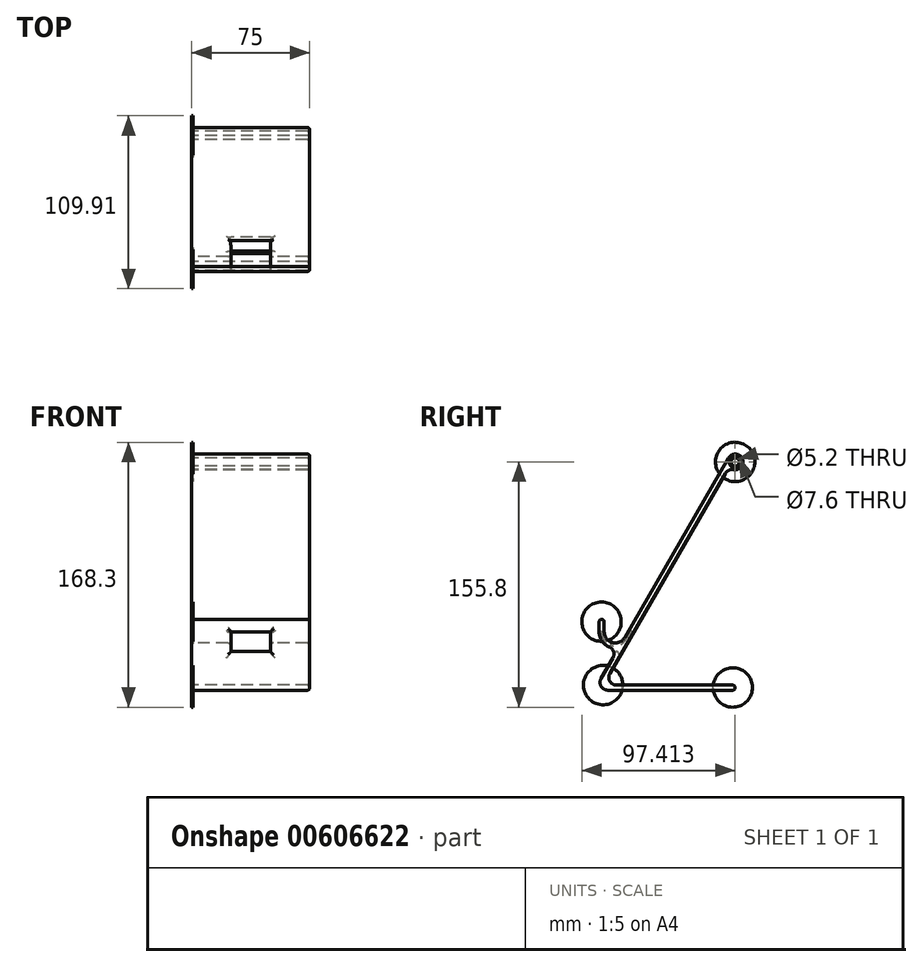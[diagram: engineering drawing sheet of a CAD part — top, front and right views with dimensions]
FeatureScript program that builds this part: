
annotation { "Feature Type Name" : "Feature", "Feature Type Description" : "" }
export const myFeature = defineFeature(function(context is Context, id is Id, definition is map)
    precondition{}
    {
        {
            var Q0;
            Q0=qCreatedBy(makeId("Right.planeOp"),FACE);
            var sketch = newSketch(context, id + "F0", { "sketchPlane" : qUnion([Q0])});
            skLineSegment(sketch, "E0.2", {"start": v(-43.92, -30) * mm, "end": v(-43.92, -38) * mm});
            skArc(sketch, "E0.4", {"start": v(-43.92, -38) * mm, "mid": v(-42.2, -43.67) * mm, "end": v(-37.61, -47.43) * mm});
            skLineSegment(sketch, "E1.2", {"start": v(-40.72, -30) * mm, "end": v(-40.72, -38) * mm});
            skLineSegment(sketch, "E1.3", {"start": v(-27.66, -41.5) * mm, "end": v(38.16, 72.5) * mm});
            skArc(sketch, "E2.filletArc", {"start": v(-40.72, -38) * mm, "mid": v(-35.53, -44.76) * mm, "end": v(-27.66, -41.5) * mm});
            skLineSegment(sketch, "E3", {"start": v(-43.92, -30) * mm, "end": v(-40.72, -30) * mm});
            skLineSegment(sketch, "E4", {"start": v(-42.67, -67.5) * mm, "end": v(-35.19, -54.55) * mm});
            skLineSegment(sketch, "E5.bottom", {"start": v(-38.34, -75) * mm, "end": v(42.5, -75) * mm});
            skLineSegment(sketch, "E5.top", {"start": v(-32.8, -71.8) * mm, "end": v(42.5, -71.8) * mm});
            skLineSegment(sketch, "E5.right", {"start": v(42.5, -75) * mm, "end": v(42.5, -71.8) * mm});
            skLineSegment(sketch, "E6", {"start": v(-37.12, -64.3) * mm, "end": v(36.2, 62.7) * mm});
            skPoint(sketch, "E7", {"position": v(0, 0) * mm});
            skArc(sketch, "E8", {"start": v(38.16, 72.5) * mm, "mid": v(47.05, 72.06) * mm, "end": v(41.51, 65.1) * mm});
            skPoint(sketch, "E9.visualSharp", {"position": v(-31.36, -47.92) * mm});
            skArc(sketch, "E9.filletArc", {"start": v(-35.19, -54.55) * mm, "mid": v(-34.79, -50.44) * mm, "end": v(-37.61, -47.43) * mm});
            skArc(sketch, "E10.filletArc", {"start": v(-37.12, -64.3) * mm, "mid": v(-37.12, -69.3) * mm, "end": v(-32.8, -71.8) * mm});
            skArc(sketch, "E11.filletArc", {"start": v(-42.67, -67.5) * mm, "mid": v(-42.67, -72.5) * mm, "end": v(-38.34, -75) * mm});
            skArc(sketch, "E12", {"start": v(41.51, 65.1) * mm, "mid": v(38.47, 64.75) * mm, "end": v(36.2, 62.7) * mm});
            skCircle(sketch, "E13", {"center": v(42.5, 70) * mm, "radius": 2.6 * mm});
            skSolve(sketch);
        }
        {
            var Q0;
            Q0=qSketchRegion(id+"F0",true);
            extrude(context, id + "F1", {"entities" : qUnion([Q0]), "endBound" : BoundingType.SYMMETRIC, "depth" : 75 * mm, "offsetDistance" : 25 * mm});
        }
        {
            var Q0;
            Q0=makeQuery(id+"F1.opExtrude","SWEPT_FACE",FACE,{"disambiguationData":[OSD([sQuery(id+"F0.wireOp",EDGE,"E0.2")])]});
            var sketch = newSketch(context, id + "F2", { "sketchPlane" : qUnion([Q0])});
            skLineSegment(sketch, "E14.bottom", {"start": v(-12.5, -38) * mm, "end": v(12.5, -38) * mm});
            skLineSegment(sketch, "E14.top", {"start": v(-12.5, -50.43) * mm, "end": v(12.5, -50.43) * mm});
            skLineSegment(sketch, "E14.left", {"start": v(-12.5, -38) * mm, "end": v(-12.5, -50.43) * mm});
            skLineSegment(sketch, "E14.right", {"start": v(12.5, -38) * mm, "end": v(12.5, -50.43) * mm});
            skSolve(sketch);
        }
        {
            var Q0;
            Q0 = qSketchRegion(id + "F2", true);
            extrude(context, id + "F3", {"entities" : qUnion([Q0]), "operationType" : NewBodyOperationType.REMOVE, "oppositeDirection" : true, "depth" : 25 * mm, "offsetDistance" : 25 * mm});
        }
        {
            var Q0;
            Q0=makeQuery(id+"F1.opExtrude","SWEPT_FACE",FACE,{"disambiguationData":[OSD([sQuery(id+"F0.wireOp",EDGE,"E3")])]});
            var Q1;
            Q1=makeQuery(id+"F1.opExtrude","CAP_FACE",FACE,{"disambiguationData":[OSD([sQuery(id+"F0.wireOp",EDGE,"E0.2"),sQuery(id+"F0.wireOp",EDGE,"E0.4"),sQuery(id+"F0.wireOp",EDGE,"E1.2"),sQuery(id+"F0.wireOp",EDGE,"E1.3"),sQuery(id+"F0.wireOp",EDGE,"E2.filletArc"),sQuery(id+"F0.wireOp",EDGE,"E3"),sQuery(id+"F0.wireOp",EDGE,"OJqH4mra-1SRE-s8op-VV3v-gDYp8EEXXtRn"),sQuery(id+"F0.wireOp",EDGE,"E4"),sQuery(id+"F0.wireOp",EDGE,"E5.bottom"),sQuery(id+"F0.wireOp",EDGE,"E5.top"),sQuery(id+"F0.wireOp",EDGE,"E5.right"),sQuery(id+"F0.wireOp",EDGE,"E6"),sQuery(id+"F0.wireOp",EDGE,"E8"),sQuery(id+"F0.wireOp",EDGE,"jVerfQlz-GGoS-WxWe-SnGt-XEWwIJdHr9bm"),sQuery(id+"F0.wireOp",EDGE,"E9.filletArc"),sQuery(id+"F0.wireOp",EDGE,"E10.filletArc"),sQuery(id+"F0.wireOp",EDGE,"E11.filletArc")])],"isStart":false});
            var Q2;
            Q2=makeQuery(id+"F1.opExtrude","CAP_FACE",FACE,{"disambiguationData":[OSD([sQuery(id+"F0.wireOp",EDGE,"E0.2"),sQuery(id+"F0.wireOp",EDGE,"E0.4"),sQuery(id+"F0.wireOp",EDGE,"E1.2"),sQuery(id+"F0.wireOp",EDGE,"E1.3"),sQuery(id+"F0.wireOp",EDGE,"E2.filletArc"),sQuery(id+"F0.wireOp",EDGE,"E3"),sQuery(id+"F0.wireOp",EDGE,"OJqH4mra-1SRE-s8op-VV3v-gDYp8EEXXtRn"),sQuery(id+"F0.wireOp",EDGE,"E4"),sQuery(id+"F0.wireOp",EDGE,"E5.bottom"),sQuery(id+"F0.wireOp",EDGE,"E5.top"),sQuery(id+"F0.wireOp",EDGE,"E5.right"),sQuery(id+"F0.wireOp",EDGE,"E6"),sQuery(id+"F0.wireOp",EDGE,"E8"),sQuery(id+"F0.wireOp",EDGE,"jVerfQlz-GGoS-WxWe-SnGt-XEWwIJdHr9bm"),sQuery(id+"F0.wireOp",EDGE,"E9.filletArc"),sQuery(id+"F0.wireOp",EDGE,"E10.filletArc"),sQuery(id+"F0.wireOp",EDGE,"E11.filletArc")])],"isStart":true});
            var Q3;
            Q3=makeQuery(id+"F1.opExtrude","SWEPT_FACE",FACE,{"disambiguationData":[OSD([sQuery(id+"F0.wireOp",EDGE,"E5.right")])]});
            var Q4;
            Q4=makeQuery(id+"F1.opExtrude","SWEPT_EDGE",EDGE,{"disambiguationData":[OSD([sQuery(id+"F0.wireOp",EDGE,"OJqH4mra-1SRE-s8op-VV3v-gDYp8EEXXtRn"),sQuery(id+"F0.wireOp",EDGE,"E8")])]});
            var Q5;
            Q5=makeQuery(id+"F1.opExtrude","SWEPT_EDGE",EDGE,{"disambiguationData":[OSD([sQuery(id+"F0.wireOp",EDGE,"OJqH4mra-1SRE-s8op-VV3v-gDYp8EEXXtRn"),sQuery(id+"F0.wireOp",EDGE,"jVerfQlz-GGoS-WxWe-SnGt-XEWwIJdHr9bm")])]});
            fillet(context, id + "F4", {"entities" : qUnion([Q0, Q1, Q2, Q3, Q4, Q5]), "radius" : 1.5 * mm, "tangentPropagation" : true, "allowEdgeOverflow" : false});
        }
        {
            var Q0;
            Q0=makeQuery(id+"F3.boolean.opBoolean","INTERSECT",EDGE,{"derivedFrom":[makeQuery(id+"F1.opExtrude","SWEPT_FACE",FACE,{"disambiguationData":[OSD([sQuery(id+"F0.wireOp",EDGE,"E9.filletArc")])]}),makeQuery(id+"F3.opExtrude","SWEPT_FACE",FACE,{"disambiguationData":[OSD([sQuery(id+"F2.wireOp",EDGE,"E14.top")])]})]});
            var Q1;
            Q1=makeQuery(id+"F3.boolean.opBoolean","INTERSECT",EDGE,{"derivedFrom":[makeQuery(id+"F1.opExtrude","SWEPT_FACE",FACE,{"disambiguationData":[OSD([sQuery(id+"F0.wireOp",EDGE,"E0.4")])]}),makeQuery(id+"F3.opExtrude","SWEPT_FACE",FACE,{"disambiguationData":[OSD([sQuery(id+"F2.wireOp",EDGE,"E14.right")])]})]});
            var Q2;
            Q2=makeQuery(id+"F3.boolean.opBoolean","INTERSECT",EDGE,{"derivedFrom":[makeQuery(id+"F1.opExtrude","SWEPT_FACE",FACE,{"disambiguationData":[OSD([sQuery(id+"F0.wireOp",EDGE,"E0.4")])]}),makeQuery(id+"F3.opExtrude","SWEPT_FACE",FACE,{"disambiguationData":[OSD([sQuery(id+"F2.wireOp",EDGE,"E14.left")])]})]});
            var Q3;
            Q3=makeQuery(id+"F3.boolean.opBoolean","MERGE",EDGE,{"derivedFrom":[makeQuery(id+"F1.opExtrude","SWEPT_EDGE",EDGE,{"disambiguationData":[OSD([sQuery(id+"F0.wireOp",EDGE,"E0.2"),sQuery(id+"F0.wireOp",EDGE,"E0.4")])]}),makeQuery(id+"F3.opExtrude","CAP_EDGE",EDGE,{"disambiguationData":[OSD([sQuery(id+"F2.wireOp",EDGE,"E14.bottom")])],"isStart":true})]});
            fillet(context, id + "F5", {"entities" : qUnion([Q0, Q1, Q2, Q3]), "radius" : 2 * mm, "tangentPropagation" : true, "allowEdgeOverflow" : false});
        }
        {
            var Q0;
            Q0=makeQuery(id+"F3.boolean.opBoolean","INTERSECT",EDGE,{"derivedFrom":[makeQuery(id+"F1.opExtrude","SWEPT_FACE",FACE,{"disambiguationData":[OSD([sQuery(id+"F0.wireOp",EDGE,"E1.3")])]}),makeQuery(id+"F3.opExtrude","SWEPT_FACE",FACE,{"disambiguationData":[OSD([sQuery(id+"F2.wireOp",EDGE,"E14.bottom")])]})]});
            var Q1;
            Q1=makeQuery(id+"F3.boolean.opBoolean","INTERSECT",EDGE,{"derivedFrom":[makeQuery(id+"F1.opExtrude","SWEPT_FACE",FACE,{"disambiguationData":[OSD([sQuery(id+"F0.wireOp",EDGE,"E2.filletArc")])]}),makeQuery(id+"F3.opExtrude","SWEPT_FACE",FACE,{"disambiguationData":[OSD([sQuery(id+"F2.wireOp",EDGE,"E14.left")])]})]});
            var Q2;
            Q2=makeQuery(id+"F3.boolean.opBoolean","INTERSECT",EDGE,{"derivedFrom":[makeQuery(id+"F1.opExtrude","SWEPT_FACE",FACE,{"disambiguationData":[OSD([sQuery(id+"F0.wireOp",EDGE,"E2.filletArc")])]}),makeQuery(id+"F3.opExtrude","SWEPT_FACE",FACE,{"disambiguationData":[OSD([sQuery(id+"F2.wireOp",EDGE,"E14.right")])]})]});
            fillet(context, id + "F6", {"entities" : qUnion([Q0, Q1, Q2]), "radius" : 2 * mm, "tangentPropagation" : true, "allowEdgeOverflow" : false});
        }
        {
            var Q0;
            Q0=makeQuery(id+"F1.opExtrude","SWEPT_FACE",FACE,{"disambiguationData":[OSD([sQuery(id+"F0.wireOp",EDGE,"E6")])]});
            fillet(context, id + "F7", {"entities" : qUnion([Q0]), "radius" : 3 * mm, "tangentPropagation" : true, "allowEdgeOverflow" : false});
        }
        {
            var Q0;
            Q0=makeQuery(id+"F1.opExtrude","CAP_FACE",FACE,{"disambiguationData":[OSD([sQuery(id+"F0.wireOp",EDGE,"E0.2"),sQuery(id+"F0.wireOp",EDGE,"E0.4"),sQuery(id+"F0.wireOp",EDGE,"E1.2"),sQuery(id+"F0.wireOp",EDGE,"E1.3"),sQuery(id+"F0.wireOp",EDGE,"E2.filletArc"),sQuery(id+"F0.wireOp",EDGE,"E3"),sQuery(id+"F0.wireOp",EDGE,"OJqH4mra-1SRE-s8op-VV3v-gDYp8EEXXtRn"),sQuery(id+"F0.wireOp",EDGE,"E4"),sQuery(id+"F0.wireOp",EDGE,"E5.bottom"),sQuery(id+"F0.wireOp",EDGE,"E5.top"),sQuery(id+"F0.wireOp",EDGE,"E5.right"),sQuery(id+"F0.wireOp",EDGE,"E6"),sQuery(id+"F0.wireOp",EDGE,"E8"),sQuery(id+"F0.wireOp",EDGE,"jVerfQlz-GGoS-WxWe-SnGt-XEWwIJdHr9bm"),sQuery(id+"F0.wireOp",EDGE,"E9.filletArc"),sQuery(id+"F0.wireOp",EDGE,"E10.filletArc"),sQuery(id+"F0.wireOp",EDGE,"E11.filletArc")])],"isStart":true});
            var sketch = newSketch(context, id + "F8", { "sketchPlane" : qUnion([Q0])});
            skCircle(sketch, "E15", {"center": v(-42.5, 70) * mm, "radius": 12.5 * mm});
            skCircle(sketch, "E16", {"center": v(-41, -73.3) * mm, "radius": 12.5 * mm});
            skCircle(sketch, "E17", {"center": v(-42.5, 70) * mm, "radius": 3.8 * mm});
            skCircle(sketch, "E18", {"center": v(41.37, -71.75) * mm, "radius": 12.5 * mm});
            skCircle(sketch, "E19", {"center": v(42.42, -31.5) * mm, "radius": 12.5 * mm});
            skSolve(sketch);
        }
        {
            var Q0;
            Q0 = qSketchRegion(id + "F8", true);
            extrude(context, id + "F9", {"entities" : qUnion([Q0]), "operationType" : NewBodyOperationType.ADD, "oppositeDirection" : true, "depth" : 1 * mm, "offsetDistance" : 25 * mm});
        }
    });
